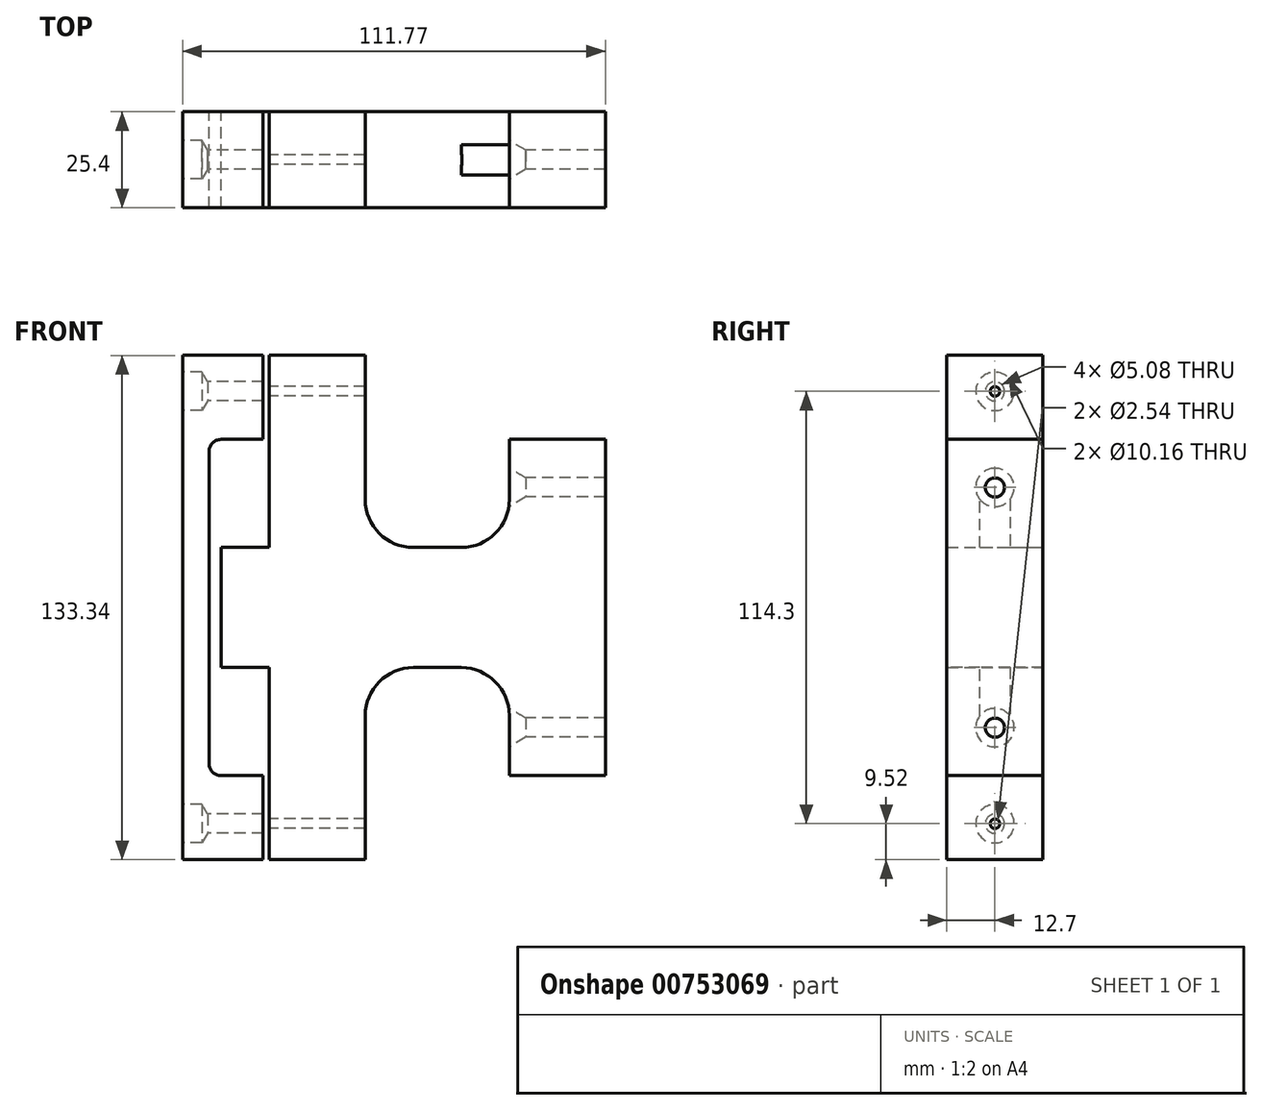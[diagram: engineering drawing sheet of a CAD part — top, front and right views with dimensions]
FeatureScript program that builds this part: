
annotation { "Feature Type Name" : "Feature", "Feature Type Description" : "" }
export const myFeature = defineFeature(function(context is Context, id is Id, definition is map)
    precondition{}
    {
        {
            var Q0;
            Q0=qCreatedBy(makeId("Front.planeOp"),FACE);
            var sketch = newSketch(context, id + "F0", { "sketchPlane" : qUnion([Q0])});
            skLineSegment(sketch, "E0", {"start": v(104.78, 40.09) * mm, "end": v(104.78, -46.03) * mm, "construction": true});
            skLineSegment(sketch, "E1", {"start": v(3.17, 41.28) * mm, "end": v(3.18, -41.28) * mm, "construction": true});
            skLineSegment(sketch, "E2", {"start": v(3.18, -41.28) * mm, "end": v(0, -41.28) * mm, "construction": true});
            skLineSegment(sketch, "E3", {"start": v(0, -41.28) * mm, "end": v(0, 41.28) * mm, "construction": true});
            skLineSegment(sketch, "E4", {"start": v(0, 41.28) * mm, "end": v(3.17, 41.28) * mm, "construction": true});
            skPoint(sketch, "E5", {"position": v(0, 0) * mm});
            skLineSegment(sketch, "E6", {"start": v(-10.16, 54.2) * mm, "end": v(-10.16, -61.27) * mm, "construction": true});
            skLineSegment(sketch, "E7.bottom", {"start": v(3.17, 41.28) * mm, "end": v(15.88, 41.28) * mm, "construction": true});
            skLineSegment(sketch, "E7.top", {"start": v(3.17, 15.88) * mm, "end": v(15.88, 15.88) * mm, "construction": true});
            skLineSegment(sketch, "E7.left", {"start": v(3.17, 41.28) * mm, "end": v(3.17, 15.88) * mm, "construction": true});
            skLineSegment(sketch, "E7.right", {"start": v(15.88, 41.28) * mm, "end": v(15.88, 15.88) * mm, "construction": true});
            skSolve(sketch);
        }
        {
            var Q0;
            Q0=qCreatedBy(makeId("Front.planeOp"),FACE);
            var sketch = newSketch(context, id + "F1", { "sketchPlane" : qUnion([Q0])});
            skLineSegment(sketch, "E8", {"start": v(104.78, 44.45) * mm, "end": v(95.25, 44.45) * mm});
            skLineSegment(sketch, "E9", {"start": v(95.25, 44.45) * mm, "end": v(95.25, 15.88) * mm});
            skLineSegment(sketch, "E10", {"start": v(95.25, -44.45) * mm, "end": v(104.78, -44.45) * mm});
            skLineSegment(sketch, "E11", {"start": v(104.78, -44.45) * mm, "end": v(104.78, 44.45) * mm});
            skPoint(sketch, "E12", {"position": v(104.78, 0) * mm});
            skLineSegment(sketch, "E13", {"start": v(95.25, 15.88) * mm, "end": v(41.28, 15.88) * mm});
            skLineSegment(sketch, "E14", {"start": v(41.28, 15.88) * mm, "end": v(41.28, 66.68) * mm});
            skLineSegment(sketch, "E15", {"start": v(41.28, 66.68) * mm, "end": v(15.88, 66.68) * mm});
            skLineSegment(sketch, "E16", {"start": v(15.88, 66.68) * mm, "end": v(15.88, 15.88) * mm});
            skLineSegment(sketch, "E17", {"start": v(15.88, 15.88) * mm, "end": v(3.18, 15.87) * mm});
            skLineSegment(sketch, "E18", {"start": v(3.18, 15.88) * mm, "end": v(3.18, -15.88) * mm});
            skLineSegment(sketch, "E19", {"start": v(3.18, -15.88) * mm, "end": v(15.88, -15.88) * mm});
            skLineSegment(sketch, "E20", {"start": v(15.88, -15.88) * mm, "end": v(15.88, -66.68) * mm});
            skLineSegment(sketch, "E21", {"start": v(15.88, -66.68) * mm, "end": v(41.28, -66.68) * mm});
            skLineSegment(sketch, "E22", {"start": v(41.28, -66.68) * mm, "end": v(41.28, -15.88) * mm});
            skLineSegment(sketch, "E23", {"start": v(41.28, -15.88) * mm, "end": v(95.25, -15.88) * mm});
            skLineSegment(sketch, "E24.trimOffspring", {"start": v(95.25, -15.88) * mm, "end": v(95.25, -44.45) * mm});
            skSolve(sketch);
        }
        {
            var Q0;
            Q0=qCreatedBy(makeId("Front.planeOp"),FACE);
            var sketch = newSketch(context, id + "F2", { "sketchPlane" : qUnion([Q0])});
            skLineSegment(sketch, "E25", {"start": v(-6.99, 66.68) * mm, "end": v(-6.98, -66.68) * mm});
            skLineSegment(sketch, "E26", {"start": v(-6.98, -66.68) * mm, "end": v(14.29, -66.68) * mm});
            skLineSegment(sketch, "E27", {"start": v(14.29, -66.68) * mm, "end": v(14.29, -44.45) * mm});
            skLineSegment(sketch, "E28", {"start": v(14.29, -44.45) * mm, "end": v(0, -44.45) * mm});
            skLineSegment(sketch, "E29", {"start": v(0, -44.45) * mm, "end": v(0, 44.45) * mm});
            skLineSegment(sketch, "E30", {"start": v(0, 44.45) * mm, "end": v(14.29, 44.45) * mm});
            skLineSegment(sketch, "E31", {"start": v(14.29, 44.45) * mm, "end": v(14.29, 66.68) * mm});
            skLineSegment(sketch, "E32", {"start": v(14.29, 66.68) * mm, "end": v(-6.99, 66.68) * mm});
            skSolve(sketch);
        }
        {
            var Q0;
            Q0 = qSketchRegion(id + "F1", true);
            extrude(context, id + "F3", {"entities" : qUnion([Q0]), "endBound" : BoundingType.SYMMETRIC, "depth" : 25.4 * mm, "offsetDistance" : 25.4 * mm});
        }
        {
            var Q0;
            Q0 = qSketchRegion(id + "F2", true);
            extrude(context, id + "F4", {"entities" : qUnion([Q0]), "endBound" : BoundingType.SYMMETRIC, "depth" : 25.4 * mm, "offsetDistance" : 25.4 * mm});
        }
        {
            var Q0;
            Q0=makeQuery(id+"F4.opExtrude","SWEPT_FACE",FACE,{"disambiguationData":[OSD([sQuery(id+"F2.wireOp",EDGE,"E25")])]});
            var sketch = newSketch(context, id + "F5", { "sketchPlane" : qUnion([Q0])});
            skPoint(sketch, "E33", {"position": v(0, 57.15) * mm});
            skPoint(sketch, "E34", {"position": v(0, -57.15) * mm});
            skSolve(sketch);
        }
        {
            var Q0;
            Q0=sQuery(id+"F5.wireOp",VERTEX,"E33");
            var Q1;
            Q1=sQuery(id+"F5.wireOp",VERTEX,"E34");
            var Q2;
            Q2=makeQuery(id+"F3.opExtrude","SWEPT_BODY",BODY,{"disambiguationData":[OSD([sQuery(id+"F1.wireOp",EDGE,"E8"),sQuery(id+"F1.wireOp",EDGE,"E9"),sQuery(id+"F1.wireOp",EDGE,"E10"),sQuery(id+"F1.wireOp",EDGE,"E11"),sQuery(id+"F1.wireOp",EDGE,"E13"),sQuery(id+"F1.wireOp",EDGE,"E14"),sQuery(id+"F1.wireOp",EDGE,"E15"),sQuery(id+"F1.wireOp",EDGE,"E16"),sQuery(id+"F1.wireOp",EDGE,"E17"),sQuery(id+"F1.wireOp",EDGE,"E18"),sQuery(id+"F1.wireOp",EDGE,"E19"),sQuery(id+"F1.wireOp",EDGE,"E20"),sQuery(id+"F1.wireOp",EDGE,"E21"),sQuery(id+"F1.wireOp",EDGE,"E22"),sQuery(id+"F1.wireOp",EDGE,"E23"),sQuery(id+"F1.wireOp",EDGE,"E24.trimOffspring")])]});
            var Q3;
            Q3=makeQuery(id+"F4.opExtrude","SWEPT_BODY",BODY,{"disambiguationData":[OSD([sQuery(id+"F2.wireOp",EDGE,"E25"),sQuery(id+"F2.wireOp",EDGE,"E26"),sQuery(id+"F2.wireOp",EDGE,"E27"),sQuery(id+"F2.wireOp",EDGE,"E28"),sQuery(id+"F2.wireOp",EDGE,"E29"),sQuery(id+"F2.wireOp",EDGE,"E30"),sQuery(id+"F2.wireOp",EDGE,"E31"),sQuery(id+"F2.wireOp",EDGE,"E32")])]});
            hole(context, id + "F6", {"style" : HoleStyle.SIMPLE, "endStyle" : HoleEndStyle.BLIND, "holeDiameter" : 10.16 * mm, "majorDiameter" : 6.35 * mm, "holeDepth" : 5.08 * mm, "isTappedThrough" : true, "tappedDepth" : 12.7 * mm, "tapClearance" : 3, "locations" : qUnion([Q0, Q1]), "scope" : qUnion([Q2, Q3])});
        }
        {
            var Q0;
            Q0=sQuery(id+"F5.wireOp",VERTEX,"E33");
            var Q1;
            Q1=sQuery(id+"F5.wireOp",VERTEX,"E34");
            var Q2;
            Q2=makeQuery(id+"F4.opExtrude","SWEPT_BODY",BODY,{"disambiguationData":[OSD([sQuery(id+"F2.wireOp",EDGE,"E25"),sQuery(id+"F2.wireOp",EDGE,"E26"),sQuery(id+"F2.wireOp",EDGE,"E27"),sQuery(id+"F2.wireOp",EDGE,"E28"),sQuery(id+"F2.wireOp",EDGE,"E29"),sQuery(id+"F2.wireOp",EDGE,"E30"),sQuery(id+"F2.wireOp",EDGE,"E31"),sQuery(id+"F2.wireOp",EDGE,"E32")])]});
            hole(context, id + "F7", {"style" : HoleStyle.C_SINK, "endStyle" : HoleEndStyle.THROUGH, "holeDiameter" : 5.08 * mm, "cSinkDiameter" : 10.16 * mm, "cSinkAngle" : 60 * degree, "majorDiameter" : 6.35 * mm, "isTappedThrough" : true, "tappedDepth" : 12.7 * mm, "tapClearance" : 3, "startFromSketch" : true, "locations" : qUnion([Q0, Q1]), "scope" : qUnion([Q2])});
        }
        {
            var Q0;
            Q0=sQuery(id+"F5.wireOp",VERTEX,"E34");
            var Q1;
            Q1=sQuery(id+"F5.wireOp",VERTEX,"E33");
            var Q2;
            Q2=makeQuery(id+"F3.opExtrude","SWEPT_BODY",BODY,{"disambiguationData":[OSD([sQuery(id+"F1.wireOp",EDGE,"E8"),sQuery(id+"F1.wireOp",EDGE,"E9"),sQuery(id+"F1.wireOp",EDGE,"E10"),sQuery(id+"F1.wireOp",EDGE,"E11"),sQuery(id+"F1.wireOp",EDGE,"E13"),sQuery(id+"F1.wireOp",EDGE,"E14"),sQuery(id+"F1.wireOp",EDGE,"E15"),sQuery(id+"F1.wireOp",EDGE,"E16"),sQuery(id+"F1.wireOp",EDGE,"E17"),sQuery(id+"F1.wireOp",EDGE,"E18"),sQuery(id+"F1.wireOp",EDGE,"E19"),sQuery(id+"F1.wireOp",EDGE,"E20"),sQuery(id+"F1.wireOp",EDGE,"E21"),sQuery(id+"F1.wireOp",EDGE,"E22"),sQuery(id+"F1.wireOp",EDGE,"E23"),sQuery(id+"F1.wireOp",EDGE,"E24.trimOffspring")])]});
            hole(context, id + "F8", {"style" : HoleStyle.SIMPLE, "endStyle" : HoleEndStyle.THROUGH, "holeDiameter" : 2.54 * mm, "majorDiameter" : 6.35 * mm, "isTappedThrough" : true, "tappedDepth" : 12.7 * mm, "tapClearance" : 3, "startFromSketch" : true, "locations" : qUnion([Q0, Q1]), "scope" : qUnion([Q2])});
        }
        {
            var Q0;
            Q0=makeQuery(id+"F3.opExtrude","SWEPT_FACE",FACE,{"disambiguationData":[OSD([sQuery(id+"F1.wireOp",EDGE,"E11")])]});
            var sketch = newSketch(context, id + "F9", { "sketchPlane" : qUnion([Q0])});
            skCircle(sketch, "E35", {"center": v(0, -31.75) * mm, "radius": 10.16 * mm});
            skCircle(sketch, "E36", {"center": v(0, 31.75) * mm, "radius": 10.16 * mm});
            skLineSegment(sketch, "E37", {"start": v(0, -31.75) * mm, "end": v(0, -44.45) * mm, "construction": true});
            skLineSegment(sketch, "E38", {"start": v(-12.7, 31.75) * mm, "end": v(0, 31.75) * mm, "construction": true});
            skLineSegment(sketch, "E39", {"start": v(0, 44.45) * mm, "end": v(0, 31.75) * mm, "construction": true});
            skLineSegment(sketch, "E40", {"start": v(12.7, -31.75) * mm, "end": v(0, -31.75) * mm, "construction": true});
            skSolve(sketch);
        }
        {
            var Q0;
            Q0 = qSketchRegion(id + "F9", true);
            extrude(context, id + "F10", {"entities" : qUnion([Q0]), "operationType" : NewBodyOperationType.ADD, "oppositeDirection" : true, "depth" : 25.4 * mm, "offsetDistance" : 25.4 * mm});
        }
        {
            var Q0;
            Q0=makeQuery(id+"F10.opExtrude","CAP_FACE",FACE,{"disambiguationData":[OSD([sQuery(id+"F9.wireOp",EDGE,"E35")])],"isStart":false});
            var sketch = newSketch(context, id + "F11", { "sketchPlane" : qUnion([Q0])});
            skPoint(sketch, "E41", {"position": v(0, -31.75) * mm});
            skPoint(sketch, "E42", {"position": v(0, 31.75) * mm});
            skSolve(sketch);
        }
        {
            var Q0;
            Q0=makeQuery(id+"F3.opExtrude","SWEPT_FACE",FACE,{"disambiguationData":[OSD([sQuery(id+"F1.wireOp",EDGE,"E11")])]});
            extrude(context, id + "F12", {"entities" : qUnion([Q0]), "operationType" : NewBodyOperationType.ADD, "oppositeDirection" : true, "depth" : 25.4 * mm, "offsetDistance" : 25.4 * mm});
        }
        {
            var Q0;
            Q0=sQuery(id+"F11.wireOp",VERTEX,"E42");
            var Q1;
            Q1=sQuery(id+"F11.wireOp",VERTEX,"E41");
            var Q2;
            Q2=makeQuery(id+"F3.opExtrude","SWEPT_BODY",BODY,{"disambiguationData":[OSD([sQuery(id+"F1.wireOp",EDGE,"E8"),sQuery(id+"F1.wireOp",EDGE,"E9"),sQuery(id+"F1.wireOp",EDGE,"E10"),sQuery(id+"F1.wireOp",EDGE,"E11"),sQuery(id+"F1.wireOp",EDGE,"E13"),sQuery(id+"F1.wireOp",EDGE,"E14"),sQuery(id+"F1.wireOp",EDGE,"E15"),sQuery(id+"F1.wireOp",EDGE,"E16"),sQuery(id+"F1.wireOp",EDGE,"E17"),sQuery(id+"F1.wireOp",EDGE,"E18"),sQuery(id+"F1.wireOp",EDGE,"E19"),sQuery(id+"F1.wireOp",EDGE,"E20"),sQuery(id+"F1.wireOp",EDGE,"E21"),sQuery(id+"F1.wireOp",EDGE,"E22"),sQuery(id+"F1.wireOp",EDGE,"E23"),sQuery(id+"F1.wireOp",EDGE,"E24.trimOffspring")])]});
            hole(context, id + "F13", {"style" : HoleStyle.C_SINK, "endStyle" : HoleEndStyle.THROUGH, "holeDiameter" : 5.08 * mm, "cSinkDiameter" : 10.16 * mm, "cSinkAngle" : 60 * degree, "majorDiameter" : 6.35 * mm, "isTappedThrough" : true, "tappedDepth" : 12.7 * mm, "tapClearance" : 3, "startFromSketch" : true, "locations" : qUnion([Q0, Q1]), "scope" : qUnion([Q2])});
        }
        {
            var Q0;
            Q0=makeQuery(id+"F12.boolean.opBoolean","INTERSECT",EDGE,{"derivedFrom":[makeQuery(id+"F3.opExtrude","SWEPT_FACE",FACE,{"disambiguationData":[OSD([sQuery(id+"F1.wireOp",EDGE,"E23")])]}),makeQuery(id+"F12.opExtrude","CAP_FACE",FACE,{"disambiguationData":[OSD([sQuery(id+"F1.wireOp",EDGE,"E11")])],"isStart":false})]});
            var Q1;
            Q1=makeQuery(id+"F3.opExtrude","SWEPT_EDGE",EDGE,{"disambiguationData":[OSD([sQuery(id+"F1.wireOp",EDGE,"E22"),sQuery(id+"F1.wireOp",EDGE,"E23")])]});
            var Q2;
            Q2=makeQuery(id+"F3.opExtrude","SWEPT_EDGE",EDGE,{"disambiguationData":[OSD([sQuery(id+"F1.wireOp",EDGE,"E13"),sQuery(id+"F1.wireOp",EDGE,"E14")])]});
            var Q3;
            Q3=makeQuery(id+"F12.boolean.opBoolean","INTERSECT",EDGE,{"derivedFrom":[makeQuery(id+"F3.opExtrude","SWEPT_FACE",FACE,{"disambiguationData":[OSD([sQuery(id+"F1.wireOp",EDGE,"E13")])]}),makeQuery(id+"F12.opExtrude","CAP_FACE",FACE,{"disambiguationData":[OSD([sQuery(id+"F1.wireOp",EDGE,"E11")])],"isStart":false})]});
            fillet(context, id + "F14", {"entities" : qUnion([Q0, Q1, Q2, Q3]), "radius" : 12.7 * mm, "tangentPropagation" : true, "allowEdgeOverflow" : false});
        }
        {
            var Q0;
            Q0=makeQuery(id+"F4.opExtrude","SWEPT_EDGE",EDGE,{"disambiguationData":[OSD([sQuery(id+"F2.wireOp",EDGE,"E28"),sQuery(id+"F2.wireOp",EDGE,"E29")])]});
            var Q1;
            Q1=makeQuery(id+"F4.opExtrude","SWEPT_EDGE",EDGE,{"disambiguationData":[OSD([sQuery(id+"F2.wireOp",EDGE,"E29"),sQuery(id+"F2.wireOp",EDGE,"E30")])]});
            fillet(context, id + "F15", {"entities" : qUnion([Q0, Q1]), "radius" : 3.17 * mm, "tangentPropagation" : true, "allowEdgeOverflow" : false});
        }
    });
